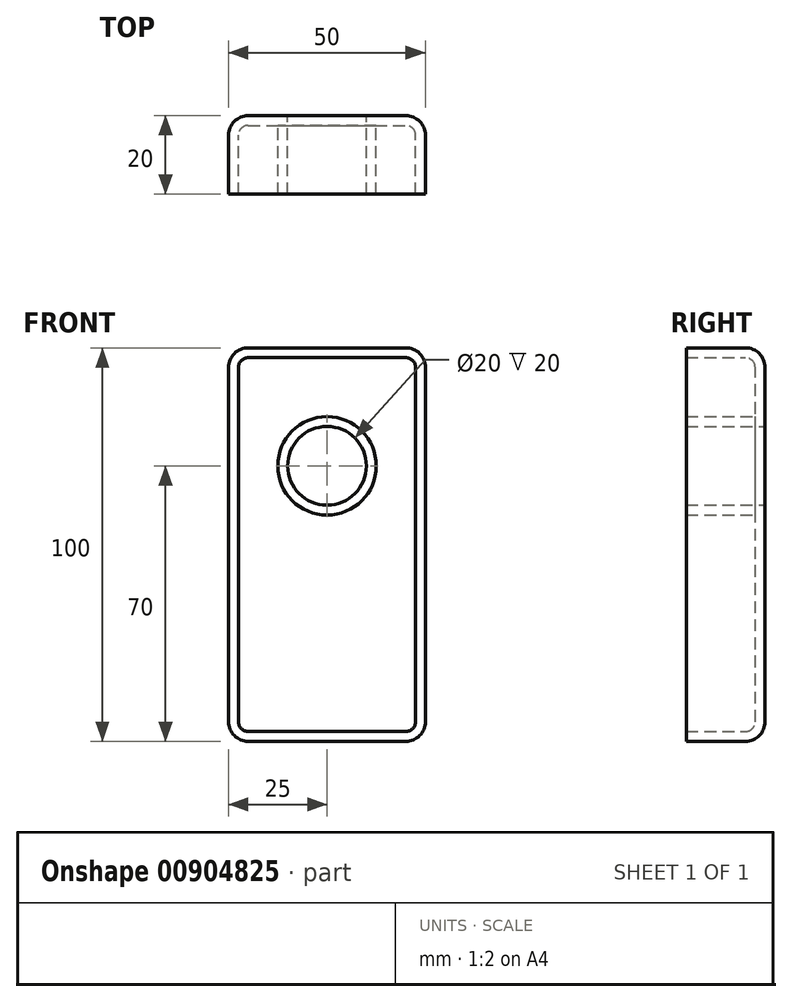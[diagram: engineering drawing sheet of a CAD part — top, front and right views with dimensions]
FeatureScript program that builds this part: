
annotation { "Feature Type Name" : "Feature", "Feature Type Description" : "" }
export const myFeature = defineFeature(function(context is Context, id is Id, definition is map)
    precondition{}
    {
        {
            var Q0;
            Q0=qCreatedBy(makeId("Front.planeOp"),FACE);
            var sketch = newSketch(context, id + "F0", { "sketchPlane" : qUnion([Q0])});
            skCircle(sketch, "E0", {"center": v(0, 0) * mm, "radius": 10 * mm});
            skCircle(sketch, "E1", {"center": v(0, 40) * mm, "radius": 10 * mm});
            skLineSegment(sketch, "E2.bottom", {"start": v(-25, 70) * mm, "end": v(25, 70) * mm});
            skLineSegment(sketch, "E2.top", {"start": v(-25, -30) * mm, "end": v(25, -30) * mm});
            skLineSegment(sketch, "E2.left", {"start": v(-25, 70) * mm, "end": v(-25, -30) * mm});
            skLineSegment(sketch, "E2.right", {"start": v(25, 70) * mm, "end": v(25, -30) * mm});
            skSolve(sketch);
        }
        {
            var Q0;
            Q0=makeQuery(id+"F0.imprint","IMPRINT",FACE,{"disambiguationData":[TD([[makeQuery(id+"F0.imprint","IMPRINT",EDGE,{"derivedFrom":sQuery(id+"F0.wireOp",EDGE,"E0")}),1.0]])]});
            var Q1;
            Q1=makeQuery(id+"F0.imprint","IMPRINT",FACE,{"disambiguationData":[TD([[makeQuery(id+"F0.imprint","IMPRINT",EDGE,{"derivedFrom":sQuery(id+"F0.wireOp",EDGE,"E0")}),-1.0]])]});
            extrude(context, id + "F1", {"entities" : qUnion([Q0, Q1]), "endBound" : BoundingType.SYMMETRIC, "depth" : 20 * mm, "offsetDistance" : 25 * mm});
        }
        {
            var Q0;
            Q0=makeQuery(id+"F1.opExtrude","SWEPT_EDGE",EDGE,{"disambiguationData":[OSD([sQuery(id+"F0.wireOp",EDGE,"E2.bottom"),sQuery(id+"F0.wireOp",EDGE,"E2.left")])]});
            var Q1;
            Q1=makeQuery(id+"F1.opExtrude","SWEPT_EDGE",EDGE,{"disambiguationData":[OSD([sQuery(id+"F0.wireOp",EDGE,"E2.bottom"),sQuery(id+"F0.wireOp",EDGE,"E2.right")])]});
            var Q2;
            Q2=makeQuery(id+"F1.opExtrude","SWEPT_EDGE",EDGE,{"disambiguationData":[OSD([sQuery(id+"F0.wireOp",EDGE,"E2.top"),sQuery(id+"F0.wireOp",EDGE,"E2.left")])]});
            var Q3;
            Q3=makeQuery(id+"F1.opExtrude","SWEPT_EDGE",EDGE,{"disambiguationData":[OSD([sQuery(id+"F0.wireOp",EDGE,"E2.top"),sQuery(id+"F0.wireOp",EDGE,"E2.right")])]});
            fillet(context, id + "F2", {"entities" : qUnion([Q0, Q1, Q2, Q3]), "radius" : 5 * mm, "tangentPropagation" : true, "allowEdgeOverflow" : false});
        }
        {
            var Q0;
            Q0=makeQuery(id+"F1.opExtrude","CAP_EDGE",EDGE,{"disambiguationData":[OSD([sQuery(id+"F0.wireOp",EDGE,"E2.bottom")])],"isStart":true});
            var Q1;
            {var subQ0=sQuery(id+"F0.wireOp",EDGE,"E2.right");var subQ1=sQuery(id+"F0.wireOp",EDGE,"E2.bottom");Q1=makeQuery(id+"F2.opFillet","BLEND_EDGE",EDGE,{"blendedFrom":[makeQuery(id+"F1.opExtrude","SWEPT_EDGE",EDGE,{"disambiguationData":[OSD([subQ1,subQ0])]}),makeQuery(id+"F1.opExtrude","CAP_FACE",FACE,{"disambiguationData":[OSD([sQuery(id+"F0.wireOp",EDGE,"E1"),subQ1,sQuery(id+"F0.wireOp",EDGE,"E2.top"),sQuery(id+"F0.wireOp",EDGE,"E2.left"),subQ0])],"isStart":true})],"blendedInto":[makeQuery(id+"F1.opExtrude","CAP_FACE",FACE,{"disambiguationData":[OSD([sQuery(id+"F0.wireOp",EDGE,"E1"),subQ1,sQuery(id+"F0.wireOp",EDGE,"E2.top"),sQuery(id+"F0.wireOp",EDGE,"E2.left"),subQ0])],"isStart":true})]});}
            var Q2;
            Q2=makeQuery(id+"F1.opExtrude","CAP_EDGE",EDGE,{"disambiguationData":[OSD([sQuery(id+"F0.wireOp",EDGE,"E2.right")])],"isStart":true});
            var Q3;
            {var subQ0=sQuery(id+"F0.wireOp",EDGE,"E2.right");var subQ1=sQuery(id+"F0.wireOp",EDGE,"E2.top");Q3=makeQuery(id+"F2.opFillet","BLEND_EDGE",EDGE,{"blendedFrom":[makeQuery(id+"F1.opExtrude","SWEPT_EDGE",EDGE,{"disambiguationData":[OSD([subQ1,subQ0])]}),makeQuery(id+"F1.opExtrude","CAP_FACE",FACE,{"disambiguationData":[OSD([sQuery(id+"F0.wireOp",EDGE,"E1"),sQuery(id+"F0.wireOp",EDGE,"E2.bottom"),subQ1,sQuery(id+"F0.wireOp",EDGE,"E2.left"),subQ0])],"isStart":true})],"blendedInto":[makeQuery(id+"F1.opExtrude","CAP_FACE",FACE,{"disambiguationData":[OSD([sQuery(id+"F0.wireOp",EDGE,"E1"),sQuery(id+"F0.wireOp",EDGE,"E2.bottom"),subQ1,sQuery(id+"F0.wireOp",EDGE,"E2.left"),subQ0])],"isStart":true})]});}
            var Q4;
            Q4=makeQuery(id+"F1.opExtrude","CAP_EDGE",EDGE,{"disambiguationData":[OSD([sQuery(id+"F0.wireOp",EDGE,"E2.top")])],"isStart":true});
            var Q5;
            {var subQ0=sQuery(id+"F0.wireOp",EDGE,"E2.left");var subQ1=sQuery(id+"F0.wireOp",EDGE,"E2.top");Q5=makeQuery(id+"F2.opFillet","BLEND_EDGE",EDGE,{"blendedFrom":[makeQuery(id+"F1.opExtrude","SWEPT_EDGE",EDGE,{"disambiguationData":[OSD([subQ1,subQ0])]}),makeQuery(id+"F1.opExtrude","CAP_FACE",FACE,{"disambiguationData":[OSD([sQuery(id+"F0.wireOp",EDGE,"E1"),sQuery(id+"F0.wireOp",EDGE,"E2.bottom"),subQ1,subQ0,sQuery(id+"F0.wireOp",EDGE,"E2.right")])],"isStart":true})],"blendedInto":[makeQuery(id+"F1.opExtrude","CAP_FACE",FACE,{"disambiguationData":[OSD([sQuery(id+"F0.wireOp",EDGE,"E1"),sQuery(id+"F0.wireOp",EDGE,"E2.bottom"),subQ1,subQ0,sQuery(id+"F0.wireOp",EDGE,"E2.right")])],"isStart":true})]});}
            var Q6;
            Q6=makeQuery(id+"F1.opExtrude","CAP_EDGE",EDGE,{"disambiguationData":[OSD([sQuery(id+"F0.wireOp",EDGE,"E2.left")])],"isStart":true});
            var Q7;
            {var subQ0=sQuery(id+"F0.wireOp",EDGE,"E2.left");var subQ1=sQuery(id+"F0.wireOp",EDGE,"E2.bottom");Q7=makeQuery(id+"F2.opFillet","BLEND_EDGE",EDGE,{"blendedFrom":[makeQuery(id+"F1.opExtrude","SWEPT_EDGE",EDGE,{"disambiguationData":[OSD([subQ1,subQ0])]}),makeQuery(id+"F1.opExtrude","CAP_FACE",FACE,{"disambiguationData":[OSD([sQuery(id+"F0.wireOp",EDGE,"E1"),subQ1,sQuery(id+"F0.wireOp",EDGE,"E2.top"),subQ0,sQuery(id+"F0.wireOp",EDGE,"E2.right")])],"isStart":true})],"blendedInto":[makeQuery(id+"F1.opExtrude","CAP_FACE",FACE,{"disambiguationData":[OSD([sQuery(id+"F0.wireOp",EDGE,"E1"),subQ1,sQuery(id+"F0.wireOp",EDGE,"E2.top"),subQ0,sQuery(id+"F0.wireOp",EDGE,"E2.right")])],"isStart":true})]});}
            fillet(context, id + "F3", {"entities" : qUnion([Q0, Q1, Q2, Q3, Q4, Q5, Q6, Q7]), "radius" : 5 * mm, "tangentPropagation" : true, "allowEdgeOverflow" : false});
        }
        {
            var Q0;
            Q0=makeQuery(id+"F1.opExtrude","CAP_FACE",FACE,{"disambiguationData":[OSD([sQuery(id+"F0.wireOp",EDGE,"E1"),sQuery(id+"F0.wireOp",EDGE,"E2.bottom"),sQuery(id+"F0.wireOp",EDGE,"E2.top"),sQuery(id+"F0.wireOp",EDGE,"E2.left"),sQuery(id+"F0.wireOp",EDGE,"E2.right")])],"isStart":false});
            shell(context, id + "F4", {"entities" : qUnion([Q0]), "thickness" : 2.5 * mm});
        }
    });
